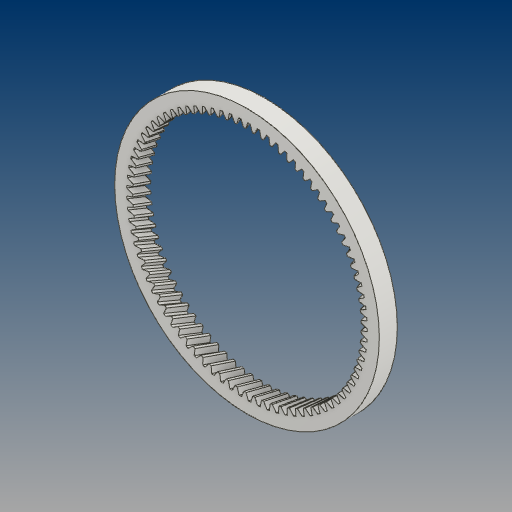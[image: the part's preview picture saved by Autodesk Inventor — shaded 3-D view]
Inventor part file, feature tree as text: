
AUTODESK INVENTOR PART (.ipt)
format: ipt  version: 2021 (Build 250183000, 183)  size: 1,070,592 bytes
history: native  units: mm (DEFAULTED — no unit token found)
features: plane x3, other x3, sketch x2, extrude x1
ambient origin geometry x8: Origin, YZ Plane, XZ Plane, XY Plane, X Axis, Y Axis, Z Axis, Center Point
bodies: Solid1 (feature_tree)
feature tree (9):
  extrude  "Extrusion1"  Depth=15.0mm TaperAngle=0.0deg
  plane  "Work Plane2"
  plane  "Work Plane8"
  plane  "Work Plane9"
  other  "Spur Gear"
  sketch  "Sketch1"  dims[d0=220.313557mm d1=15.0mm d2=0.0mm]
  sketch  "Sketch2"  dims[d3=193.946399mm d4=10.0mm d5=0.0mm d16=65.0mm d17=0.0mm d34=0.387851mm d39=0.0mm d45=0.0mm d47=65.0mm d50=0.0mm d51=0.0mm d52=65.0mm]
  other  "Srf1"
  other  "Pitch Diameter"
